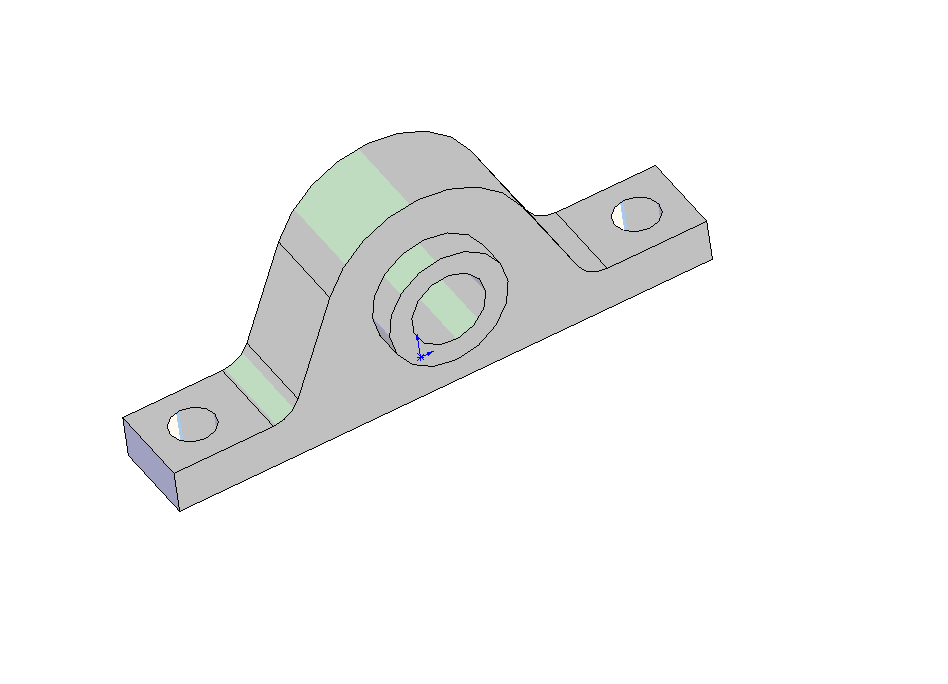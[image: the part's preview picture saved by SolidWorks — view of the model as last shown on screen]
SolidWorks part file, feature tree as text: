
SOLIDWORKS PART (.sldprt)
format: sldprt  version: not decoded by parser v0  size: 117,760 bytes
history: native  units: mm
features: sketch x3, cut_extrude x2, material x1, extrude x1, fillet x1 (+13 scaffold rows collapsed)
feature tree (21):
  scaffold x13  (default folders/planes/origin — collapsed)
  material  "Material <not specified>"
  sketch  "Sketch1"  dims[D1=50.8mm D2=33.3375mm D3=12.7mm D4=63.5mm D5=127.0mm]
  extrude  "Extrude1"  Depth=36.5125mm
  fillet  "Fillet1"  Radius=6.35mm
  sketch  "Sketch3"  dims[D1=~7.198219mm D2=33.3375mm]
  cut_extrude  "Cut-Extrude1"  [1 undecoded]
  sketch  "Sketch4"  dims[D1=11.1125mm D2=95.25mm]
  cut_extrude  "Cut-Extrude2"  [1 undecoded]
decode coverage: 5 of 7 modeling features carry decoded parameters
note: ~ marks probable driven/reference dimensions
note: 2 parameter values undecoded
note: suppression state not decoded; provenance and decode notes live in map.json
